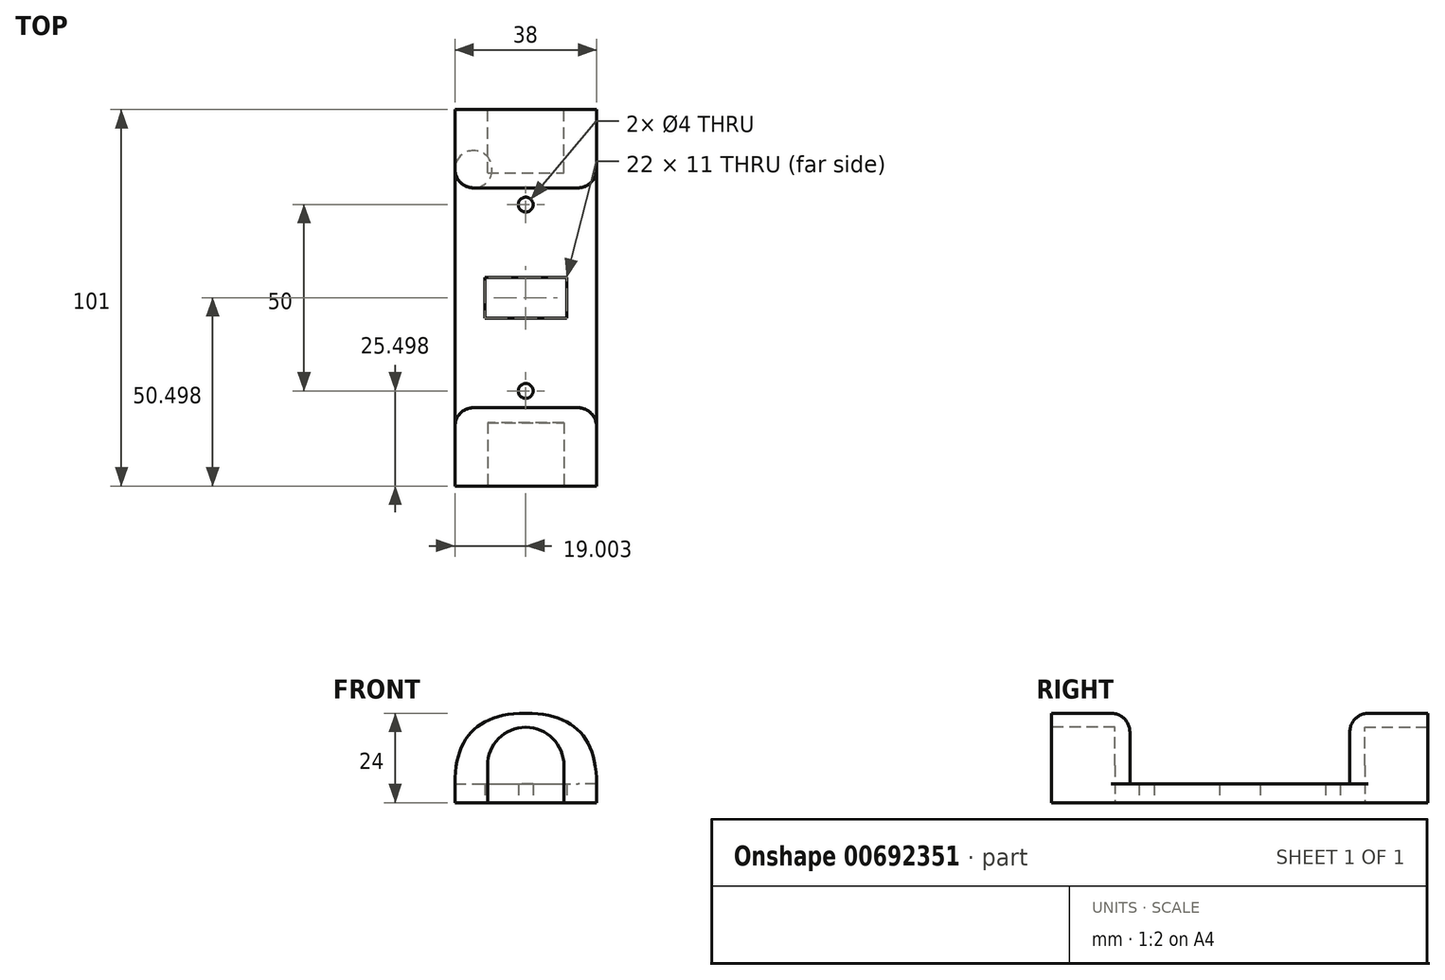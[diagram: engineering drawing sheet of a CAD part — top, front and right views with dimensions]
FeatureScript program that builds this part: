
annotation { "Feature Type Name" : "Feature", "Feature Type Description" : "" }
export const myFeature = defineFeature(function(context is Context, id is Id, definition is map)
    precondition{}
    {
        {
            var Q0;
            Q0=qCreatedBy(makeId("Top.planeOp"),FACE);
            var sketch = newSketch(context, id + "F0", { "sketchPlane" : qUnion([Q0])});
            skLineSegment(sketch, "E0.bottom", {"start": v(-20.75, 70.16) * mm, "end": v(17.25, 70.16) * mm});
            skLineSegment(sketch, "E0.top", {"start": v(-20.75, -30.84) * mm, "end": v(17.25, -30.84) * mm});
            skLineSegment(sketch, "E0.left", {"start": v(-20.75, 70.16) * mm, "end": v(-20.75, -30.84) * mm});
            skLineSegment(sketch, "E0.right", {"start": v(17.25, 70.16) * mm, "end": v(17.25, -30.84) * mm});
            skLineSegment(sketch, "E1", {"start": v(-12.75, 70.16) * mm, "end": v(-12.75, -30.84) * mm});
            skLineSegment(sketch, "E2", {"start": v(9.25, 70.16) * mm, "end": v(9.25, -30.84) * mm});
            skLineSegment(sketch, "E3", {"start": v(-20.75, 53.16) * mm, "end": v(17.25, 53.16) * mm});
            skLineSegment(sketch, "E4", {"start": v(-20.75, -13.84) * mm, "end": v(17.25, -13.84) * mm});
            skLineSegment(sketch, "E5", {"start": v(-20.75, 25.16) * mm, "end": v(17.25, 25.16) * mm});
            skLineSegment(sketch, "E6", {"start": v(-20.75, 14.16) * mm, "end": v(17.25, 14.16) * mm});
            skLineSegment(sketch, "E7", {"start": v(-1.75, 70.16) * mm, "end": v(-1.75, -30.84) * mm, "construction": true});
            skCircle(sketch, "E8", {"center": v(-1.75, 44.66) * mm, "radius": 2 * mm});
            skCircle(sketch, "E9", {"center": v(-1.75, -5.34) * mm, "radius": 2 * mm});
            skLineSegment(sketch, "E10", {"start": v(-20.75, 49.16) * mm, "end": v(17.25, 49.16) * mm});
            skLineSegment(sketch, "E11", {"start": v(-20.75, -9.84) * mm, "end": v(17.25, -9.84) * mm});
            skSolve(sketch);
        }
        {
            var Q0;
            Q0=makeQuery(id+"F0.imprint","IMPRINT",FACE,{"disambiguationData":[TD([[makeQuery(id+"F0.imprint","IMPRINT",EDGE,{"derivedFrom":sQuery(id+"F0.wireOp",EDGE,"E8")}),-1.0]])]});
            var Q1;
            {var subQ0=sQuery(id+"F0.wireOp",EDGE,"E5");var subQ1=sQuery(id+"F0.wireOp",EDGE,"E0.right");var subQ2=makeQuery(id+"F0.imprint","INTERSECT",VERTEX,{"derivedFrom":[subQ1,subQ0]});Q1=makeQuery(id+"F0.imprint","IMPRINT",FACE,{"disambiguationData":[TD([[makeQuery(id+"F0.imprint","IMPRINT",EDGE,{"disambiguationData":[TD([[subQ2,-1.0]])],"derivedFrom":subQ1}),-1.0]])]});}
            var Q2;
            {var subQ0=sQuery(id+"F0.wireOp",EDGE,"E5");var subQ1=sQuery(id+"F0.wireOp",EDGE,"E0.left");var subQ2=makeQuery(id+"F0.imprint","INTERSECT",VERTEX,{"derivedFrom":[subQ1,subQ0]});Q2=makeQuery(id+"F0.imprint","IMPRINT",FACE,{"disambiguationData":[TD([[makeQuery(id+"F0.imprint","IMPRINT",EDGE,{"disambiguationData":[TD([[subQ2,-1.0]])],"derivedFrom":subQ1}),1.0]])]});}
            var Q3;
            Q3=makeQuery(id+"F0.imprint","IMPRINT",FACE,{"disambiguationData":[TD([[makeQuery(id+"F0.imprint","IMPRINT",EDGE,{"derivedFrom":sQuery(id+"F0.wireOp",EDGE,"E9")}),-1.0]])]});
            var Q4;
            {var subQ0=sQuery(id+"F0.wireOp",EDGE,"E5");var subQ1=sQuery(id+"F0.wireOp",EDGE,"E0.left");var subQ2=makeQuery(id+"F0.imprint","INTERSECT",VERTEX,{"derivedFrom":[subQ1,subQ0]});Q4=makeQuery(id+"F0.imprint","IMPRINT",FACE,{"disambiguationData":[TD([[makeQuery(id+"F0.imprint","IMPRINT",EDGE,{"disambiguationData":[TD([[subQ2,1.0]])],"derivedFrom":subQ1}),1.0]])]});}
            var Q5;
            {var subQ0=sQuery(id+"F0.wireOp",EDGE,"E5");var subQ1=sQuery(id+"F0.wireOp",EDGE,"E0.right");var subQ2=makeQuery(id+"F0.imprint","INTERSECT",VERTEX,{"derivedFrom":[subQ1,subQ0]});Q5=makeQuery(id+"F0.imprint","IMPRINT",FACE,{"disambiguationData":[TD([[makeQuery(id+"F0.imprint","IMPRINT",EDGE,{"disambiguationData":[TD([[subQ2,1.0]])],"derivedFrom":subQ1}),-1.0]])]});}
            var Q6;
            {var subQ0=sQuery(id+"F0.wireOp",EDGE,"E6");var subQ1=sQuery(id+"F0.wireOp",EDGE,"E0.right");var subQ2=makeQuery(id+"F0.imprint","INTERSECT",VERTEX,{"derivedFrom":[subQ1,subQ0]});Q6=makeQuery(id+"F0.imprint","IMPRINT",FACE,{"disambiguationData":[TD([[makeQuery(id+"F0.imprint","IMPRINT",EDGE,{"disambiguationData":[TD([[subQ2,-1.0]])],"derivedFrom":subQ1}),-1.0]])]});}
            var Q7;
            {var subQ0=sQuery(id+"F0.wireOp",EDGE,"E6");var subQ1=sQuery(id+"F0.wireOp",EDGE,"E0.left");var subQ2=makeQuery(id+"F0.imprint","INTERSECT",VERTEX,{"derivedFrom":[subQ1,subQ0]});Q7=makeQuery(id+"F0.imprint","IMPRINT",FACE,{"disambiguationData":[TD([[makeQuery(id+"F0.imprint","IMPRINT",EDGE,{"disambiguationData":[TD([[subQ2,-1.0]])],"derivedFrom":subQ1}),1.0]])]});}
            extrude(context, id + "F1", {"entities" : qUnion([Q0, Q1, Q2, Q3, Q4, Q5, Q6, Q7]), "depth" : 5 * mm, "offsetDistance" : 25 * mm});
        }
        {
            var Q0;
            {var subQ0=sQuery(id+"F0.wireOp",EDGE,"E3");var subQ1=sQuery(id+"F0.wireOp",EDGE,"E0.left");var subQ2=makeQuery(id+"F0.imprint","INTERSECT",VERTEX,{"derivedFrom":[subQ1,subQ0]});Q0=makeQuery(id+"F0.imprint","IMPRINT",FACE,{"disambiguationData":[TD([[makeQuery(id+"F0.imprint","IMPRINT",EDGE,{"disambiguationData":[TD([[subQ2,-1.0]])],"derivedFrom":subQ1}),1.0]])]});}
            var Q1;
            {var subQ0=sQuery(id+"F0.wireOp",EDGE,"E0.left");var subQ1=sQuery(id+"F0.wireOp",EDGE,"E0.bottom");var subQ2=makeQuery(id+"F0.imprint","INTERSECT",VERTEX,{"derivedFrom":[subQ1,subQ0]});Q1=makeQuery(id+"F0.imprint","IMPRINT",FACE,{"disambiguationData":[TD([[makeQuery(id+"F0.imprint","IMPRINT",EDGE,{"disambiguationData":[TD([[subQ2,-1.0]])],"derivedFrom":subQ1}),-1.0]])]});}
            var Q2;
            {var subQ0=sQuery(id+"F0.wireOp",EDGE,"E3");var subQ1=sQuery(id+"F0.wireOp",EDGE,"E1");var subQ2=makeQuery(id+"F0.imprint","INTERSECT",VERTEX,{"derivedFrom":[subQ1,subQ0]});Q2=makeQuery(id+"F0.imprint","IMPRINT",FACE,{"disambiguationData":[TD([[makeQuery(id+"F0.imprint","IMPRINT",EDGE,{"disambiguationData":[TD([[subQ2,-1.0]])],"derivedFrom":subQ1}),1.0]])]});}
            var Q3;
            {var subQ0=sQuery(id+"F0.wireOp",EDGE,"E3");var subQ1=sQuery(id+"F0.wireOp",EDGE,"E0.right");var subQ2=makeQuery(id+"F0.imprint","INTERSECT",VERTEX,{"derivedFrom":[subQ1,subQ0]});Q3=makeQuery(id+"F0.imprint","IMPRINT",FACE,{"disambiguationData":[TD([[makeQuery(id+"F0.imprint","IMPRINT",EDGE,{"disambiguationData":[TD([[subQ2,-1.0]])],"derivedFrom":subQ1}),-1.0]])]});}
            var Q4;
            {var subQ0=sQuery(id+"F0.wireOp",EDGE,"E0.right");var subQ1=sQuery(id+"F0.wireOp",EDGE,"E0.bottom");var subQ2=makeQuery(id+"F0.imprint","INTERSECT",VERTEX,{"derivedFrom":[subQ1,subQ0]});Q4=makeQuery(id+"F0.imprint","IMPRINT",FACE,{"disambiguationData":[TD([[makeQuery(id+"F0.imprint","IMPRINT",EDGE,{"disambiguationData":[TD([[subQ2,1.0]])],"derivedFrom":subQ1}),-1.0]])]});}
            var Q5;
            {var subQ0=sQuery(id+"F0.wireOp",EDGE,"E4");var subQ1=sQuery(id+"F0.wireOp",EDGE,"E0.left");var subQ2=makeQuery(id+"F0.imprint","INTERSECT",VERTEX,{"derivedFrom":[subQ1,subQ0]});Q5=makeQuery(id+"F0.imprint","IMPRINT",FACE,{"disambiguationData":[TD([[makeQuery(id+"F0.imprint","IMPRINT",EDGE,{"disambiguationData":[TD([[subQ2,1.0]])],"derivedFrom":subQ1}),1.0]])]});}
            var Q6;
            {var subQ0=sQuery(id+"F0.wireOp",EDGE,"E0.left");var subQ1=sQuery(id+"F0.wireOp",EDGE,"E0.top");var subQ2=makeQuery(id+"F0.imprint","INTERSECT",VERTEX,{"derivedFrom":[subQ1,subQ0]});Q6=makeQuery(id+"F0.imprint","IMPRINT",FACE,{"disambiguationData":[TD([[makeQuery(id+"F0.imprint","IMPRINT",EDGE,{"disambiguationData":[TD([[subQ2,-1.0]])],"derivedFrom":subQ1}),1.0]])]});}
            var Q7;
            {var subQ0=sQuery(id+"F0.wireOp",EDGE,"E4");var subQ1=sQuery(id+"F0.wireOp",EDGE,"E0.right");var subQ2=makeQuery(id+"F0.imprint","INTERSECT",VERTEX,{"derivedFrom":[subQ1,subQ0]});Q7=makeQuery(id+"F0.imprint","IMPRINT",FACE,{"disambiguationData":[TD([[makeQuery(id+"F0.imprint","IMPRINT",EDGE,{"disambiguationData":[TD([[subQ2,1.0]])],"derivedFrom":subQ1}),-1.0]])]});}
            var Q8;
            {var subQ0=sQuery(id+"F0.wireOp",EDGE,"E0.right");var subQ1=sQuery(id+"F0.wireOp",EDGE,"E0.top");var subQ2=makeQuery(id+"F0.imprint","INTERSECT",VERTEX,{"derivedFrom":[subQ1,subQ0]});Q8=makeQuery(id+"F0.imprint","IMPRINT",FACE,{"disambiguationData":[TD([[makeQuery(id+"F0.imprint","IMPRINT",EDGE,{"disambiguationData":[TD([[subQ2,1.0]])],"derivedFrom":subQ1}),1.0]])]});}
            var Q9;
            {var subQ0=sQuery(id+"F0.wireOp",EDGE,"E11");var subQ1=sQuery(id+"F0.wireOp",EDGE,"E1");var subQ2=makeQuery(id+"F0.imprint","INTERSECT",VERTEX,{"derivedFrom":[subQ1,subQ0]});Q9=makeQuery(id+"F0.imprint","IMPRINT",FACE,{"disambiguationData":[TD([[makeQuery(id+"F0.imprint","IMPRINT",EDGE,{"disambiguationData":[TD([[subQ2,-1.0]])],"derivedFrom":subQ1}),1.0]])]});}
            var Q10;
            {var subQ0=sQuery(id+"F0.wireOp",EDGE,"E1");var subQ1=sQuery(id+"F0.wireOp",EDGE,"E0.top");var subQ2=makeQuery(id+"F0.imprint","INTERSECT",VERTEX,{"derivedFrom":[subQ1,subQ0]});Q10=makeQuery(id+"F0.imprint","IMPRINT",FACE,{"disambiguationData":[TD([[makeQuery(id+"F0.imprint","IMPRINT",EDGE,{"disambiguationData":[TD([[subQ2,-1.0]])],"derivedFrom":subQ1}),1.0]])]});}
            var Q11;
            {var subQ0=sQuery(id+"F0.wireOp",EDGE,"E1");var subQ1=sQuery(id+"F0.wireOp",EDGE,"E0.bottom");var subQ2=makeQuery(id+"F0.imprint","INTERSECT",VERTEX,{"derivedFrom":[subQ1,subQ0]});Q11=makeQuery(id+"F0.imprint","IMPRINT",FACE,{"disambiguationData":[TD([[makeQuery(id+"F0.imprint","IMPRINT",EDGE,{"disambiguationData":[TD([[subQ2,-1.0]])],"derivedFrom":subQ1}),-1.0]])]});}
            extrude(context, id + "F2", {"entities" : qUnion([Q0, Q1, Q2, Q3, Q4, Q5, Q6, Q7, Q8, Q9, Q10, Q11]), "operationType" : NewBodyOperationType.ADD, "depth" : 24 * mm, "offsetDistance" : 25 * mm});
        }
        {
            var Q0;
            Q0=makeQuery(id+"F2.opExtrude","SWEPT_FACE",FACE,{"disambiguationData":[OSD([sQuery(id+"F0.wireOp",EDGE,"E0.bottom")])]});
            var sketch = newSketch(context, id + "F3", { "sketchPlane" : qUnion([Q0])});
            skLineSegment(sketch, "E12", {"start": v(1.75, 24) * mm, "end": v(1.75, 0) * mm, "construction": true});
            skCircle(sketch, "E13", {"center": v(1.75, 10) * mm, "radius": 10.25 * mm});
            skLineSegment(sketch, "E14", {"start": v(-8.5, 10) * mm, "end": v(-8.5, 0) * mm});
            skLineSegment(sketch, "E15", {"start": v(12, 10) * mm, "end": v(12, 0) * mm});
            skSolve(sketch);
        }
        {
            var Q0;
            Q0=makeQuery(id+"F2.opExtrude","SWEPT_FACE",FACE,{"disambiguationData":[OSD([sQuery(id+"F0.wireOp",EDGE,"E0.top")])]});
            var sketch = newSketch(context, id + "F4", { "sketchPlane" : qUnion([Q0])});
            skLineSegment(sketch, "E16", {"start": v(-1.75, 24) * mm, "end": v(-1.75, 0) * mm, "construction": true});
            skCircle(sketch, "E17", {"center": v(-1.75, 10) * mm, "radius": 10.25 * mm});
            skLineSegment(sketch, "E18", {"start": v(-12, 10) * mm, "end": v(-12, 0) * mm});
            skLineSegment(sketch, "E19", {"start": v(8.5, 10) * mm, "end": v(8.5, 0) * mm});
            skSolve(sketch);
        }
        {
            var Q0;
            {var subQ0=sQuery(id+"F3.wireOp",EDGE,"E13");var subQ1=makeQuery(id+"F3.imprint","INTERSECT",VERTEX,{"derivedFrom":[subQ0,sQuery(id+"F3.wireOp",EDGE,"E14")]});Q0=makeQuery(id+"F3.imprint","IMPRINT",FACE,{"disambiguationData":[TD([[makeQuery(id+"F3.imprint","IMPRINT",EDGE,{"disambiguationData":[TD([[subQ1,1.0]])],"derivedFrom":subQ0}),1.0]])]});}
            var Q1;
            {var subQ0=sQuery(id+"F3.wireOp",EDGE,"E15");Q1=makeQuery(id+"F3.imprint","IMPRINT",FACE,{"disambiguationData":[TD([[makeQuery(id+"F3.imprint","IMPRINT",EDGE,{"derivedFrom":subQ0}),-1.0]])]});}
            var Q2;
            {var subQ0=sQuery(id+"F3.wireOp",EDGE,"E14");Q2=makeQuery(id+"F3.imprint","IMPRINT",FACE,{"disambiguationData":[TD([[makeQuery(id+"F3.imprint","IMPRINT",EDGE,{"derivedFrom":subQ0}),1.0]])]});}
            extrude(context, id + "F5", {"entities" : qUnion([Q0, Q1, Q2]), "operationType" : NewBodyOperationType.REMOVE, "oppositeDirection" : true, "depth" : 17 * mm, "offsetDistance" : 25 * mm});
        }
        {
            var Q0;
            {var subQ0=sQuery(id+"F4.wireOp",EDGE,"E17");var subQ1=makeQuery(id+"F4.imprint","INTERSECT",VERTEX,{"derivedFrom":[subQ0,sQuery(id+"F4.wireOp",EDGE,"E18")]});Q0=makeQuery(id+"F4.imprint","IMPRINT",FACE,{"disambiguationData":[TD([[makeQuery(id+"F4.imprint","IMPRINT",EDGE,{"disambiguationData":[TD([[subQ1,1.0]])],"derivedFrom":subQ0}),1.0]])]});}
            var Q1;
            {var subQ0=sQuery(id+"F4.wireOp",EDGE,"E18");Q1=makeQuery(id+"F4.imprint","IMPRINT",FACE,{"disambiguationData":[TD([[makeQuery(id+"F4.imprint","IMPRINT",EDGE,{"derivedFrom":subQ0}),1.0]])]});}
            var Q2;
            {var subQ0=sQuery(id+"F4.wireOp",EDGE,"E19");Q2=makeQuery(id+"F4.imprint","IMPRINT",FACE,{"disambiguationData":[TD([[makeQuery(id+"F4.imprint","IMPRINT",EDGE,{"derivedFrom":subQ0}),-1.0]])]});}
            extrude(context, id + "F6", {"entities" : qUnion([Q0, Q1, Q2]), "operationType" : NewBodyOperationType.REMOVE, "oppositeDirection" : true, "depth" : 17 * mm, "offsetDistance" : 25 * mm});
        }
        {
            var Q0;
            {var subQ0=sQuery(id+"F0.wireOp",EDGE,"E0.right");var subQ1=makeQuery(id+"F0.imprint","INTERSECT",VERTEX,{"derivedFrom":[subQ0,sQuery(id+"F0.wireOp",EDGE,"E4")]});Q0=makeQuery(id+"F2.opExtrude","CAP_EDGE",EDGE,{"disambiguationData":[OSD([subQ0]),TDD([makeQuery(id+"F0.imprint","IMPRINT",EDGE,{"disambiguationData":[TD([[subQ1,1.0]])],"derivedFrom":subQ0}),makeQuery(id+"F0.imprint","IMPRINT",EDGE,{"disambiguationData":[TD([[makeQuery(id+"F0.imprint","INTERSECT",VERTEX,{"derivedFrom":[sQuery(id+"F0.wireOp",EDGE,"E0.top"),subQ0]}),1.0]])],"derivedFrom":subQ0})])],"isStart":false});}
            var Q1;
            {var subQ0=sQuery(id+"F0.wireOp",EDGE,"E0.right");var subQ1=makeQuery(id+"F0.imprint","INTERSECT",VERTEX,{"derivedFrom":[subQ0,sQuery(id+"F0.wireOp",EDGE,"E3")]});Q1=makeQuery(id+"F2.opExtrude","CAP_EDGE",EDGE,{"disambiguationData":[OSD([subQ0]),TDD([makeQuery(id+"F0.imprint","IMPRINT",EDGE,{"disambiguationData":[TD([[makeQuery(id+"F0.imprint","INTERSECT",VERTEX,{"derivedFrom":[sQuery(id+"F0.wireOp",EDGE,"E0.bottom"),subQ0]}),-1.0]])],"derivedFrom":subQ0}),makeQuery(id+"F0.imprint","IMPRINT",EDGE,{"disambiguationData":[TD([[subQ1,-1.0]])],"derivedFrom":subQ0})])],"isStart":false});}
            var Q2;
            {var subQ0=sQuery(id+"F0.wireOp",EDGE,"E0.left");var subQ1=makeQuery(id+"F0.imprint","INTERSECT",VERTEX,{"derivedFrom":[subQ0,sQuery(id+"F0.wireOp",EDGE,"E4")]});Q2=makeQuery(id+"F2.opExtrude","CAP_EDGE",EDGE,{"disambiguationData":[OSD([subQ0]),TDD([makeQuery(id+"F0.imprint","IMPRINT",EDGE,{"disambiguationData":[TD([[subQ1,1.0]])],"derivedFrom":subQ0}),makeQuery(id+"F0.imprint","IMPRINT",EDGE,{"disambiguationData":[TD([[makeQuery(id+"F0.imprint","INTERSECT",VERTEX,{"derivedFrom":[sQuery(id+"F0.wireOp",EDGE,"E0.top"),subQ0]}),1.0]])],"derivedFrom":subQ0})])],"isStart":false});}
            var Q3;
            {var subQ0=sQuery(id+"F0.wireOp",EDGE,"E0.left");var subQ1=makeQuery(id+"F0.imprint","INTERSECT",VERTEX,{"derivedFrom":[subQ0,sQuery(id+"F0.wireOp",EDGE,"E3")]});Q3=makeQuery(id+"F2.opExtrude","CAP_EDGE",EDGE,{"disambiguationData":[OSD([subQ0]),TDD([makeQuery(id+"F0.imprint","IMPRINT",EDGE,{"disambiguationData":[TD([[makeQuery(id+"F0.imprint","INTERSECT",VERTEX,{"derivedFrom":[sQuery(id+"F0.wireOp",EDGE,"E0.bottom"),subQ0]}),-1.0]])],"derivedFrom":subQ0}),makeQuery(id+"F0.imprint","IMPRINT",EDGE,{"disambiguationData":[TD([[subQ1,-1.0]])],"derivedFrom":subQ0})])],"isStart":false});}
            fillet(context, id + "F7", {"entities" : qUnion([Q0, Q1, Q2, Q3]), "radius" : 18.9 * mm, "tangentPropagation" : true, "rho" : 0.5, "crossSection" : FilletCrossSection.CONIC, "allowEdgeOverflow" : false});
        }
        {
            var Q0;
            {var subQ0=sQuery(id+"F0.wireOp",EDGE,"E10");var subQ1=sQuery(id+"F0.wireOp",EDGE,"E0.left");var subQ2=makeQuery(id+"F0.imprint","INTERSECT",VERTEX,{"derivedFrom":[subQ1,sQuery(id+"F0.wireOp",EDGE,"E3")]});Q0=makeQuery(id+"F7.opFillet","BLEND_EDGE",EDGE,{"blendedFrom":[makeQuery(id+"F2.opExtrude","CAP_EDGE",EDGE,{"disambiguationData":[OSD([subQ1]),TDD([makeQuery(id+"F0.imprint","IMPRINT",EDGE,{"disambiguationData":[TD([[makeQuery(id+"F0.imprint","INTERSECT",VERTEX,{"derivedFrom":[sQuery(id+"F0.wireOp",EDGE,"E0.bottom"),subQ1]}),-1.0]])],"derivedFrom":subQ1}),makeQuery(id+"F0.imprint","IMPRINT",EDGE,{"disambiguationData":[TD([[subQ2,-1.0]])],"derivedFrom":subQ1})])],"isStart":false}),makeQuery(id+"F2.opExtrude","SWEPT_FACE",FACE,{"disambiguationData":[OSD([subQ0])]})],"blendedInto":[makeQuery(id+"F2.opExtrude","SWEPT_FACE",FACE,{"disambiguationData":[OSD([subQ0])]})]});}
            var Q1;
            {var subQ0=sQuery(id+"F0.wireOp",EDGE,"E11");var subQ1=sQuery(id+"F0.wireOp",EDGE,"E0.left");var subQ2=makeQuery(id+"F0.imprint","INTERSECT",VERTEX,{"derivedFrom":[subQ1,sQuery(id+"F0.wireOp",EDGE,"E4")]});Q1=makeQuery(id+"F7.opFillet","BLEND_EDGE",EDGE,{"blendedFrom":[makeQuery(id+"F2.opExtrude","CAP_EDGE",EDGE,{"disambiguationData":[OSD([subQ1]),TDD([makeQuery(id+"F0.imprint","IMPRINT",EDGE,{"disambiguationData":[TD([[subQ2,1.0]])],"derivedFrom":subQ1}),makeQuery(id+"F0.imprint","IMPRINT",EDGE,{"disambiguationData":[TD([[makeQuery(id+"F0.imprint","INTERSECT",VERTEX,{"derivedFrom":[sQuery(id+"F0.wireOp",EDGE,"E0.top"),subQ1]}),1.0]])],"derivedFrom":subQ1})])],"isStart":false}),makeQuery(id+"F2.opExtrude","SWEPT_FACE",FACE,{"disambiguationData":[OSD([subQ0])]})],"blendedInto":[makeQuery(id+"F2.opExtrude","SWEPT_FACE",FACE,{"disambiguationData":[OSD([subQ0])]})]});}
            fillet(context, id + "F8", {"entities" : qUnion([Q0, Q1]), "radius" : 5 * mm, "tangentPropagation" : true, "allowEdgeOverflow" : false});
        }
    });
